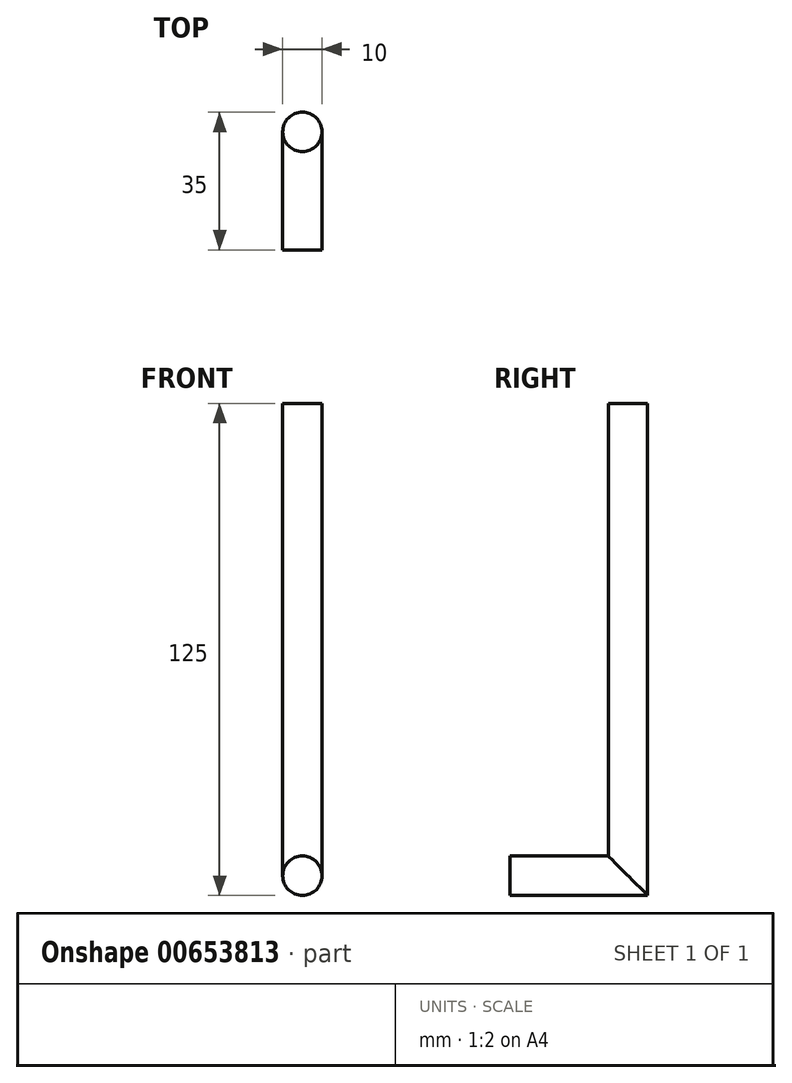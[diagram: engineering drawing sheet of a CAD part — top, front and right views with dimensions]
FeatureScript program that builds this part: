
annotation { "Feature Type Name" : "Feature", "Feature Type Description" : "" }
export const myFeature = defineFeature(function(context is Context, id is Id, definition is map)
    precondition{}
    {
        {
            var Q0;
            Q0=qCreatedBy(makeId("Right.planeOp"),FACE);
            var sketch = newSketch(context, id + "F0", { "sketchPlane" : qUnion([Q0])});
            skLineSegment(sketch, "E0", {"start": v(0, 0) * mm, "end": v(30, 0) * mm});
            skLineSegment(sketch, "E1", {"start": v(30, 0) * mm, "end": v(30, 120) * mm});
            skSolve(sketch);
        }
        {
            var Q0;
            Q0=qCreatedBy(makeId("Front.planeOp"),FACE);
            var sketch = newSketch(context, id + "F1", { "sketchPlane" : qUnion([Q0])});
            skCircle(sketch, "E2", {"center": v(0, 0) * mm, "radius": 5 * mm});
            skSolve(sketch);
        }
        {
            var Q0;
            Q0 = qSketchRegion(id + "F0", true);
            var Q1;
            Q1=makeQuery(id+"F1.imprint","IMPRINT",FACE,{"disambiguationData":[TD([[makeQuery(id+"F1.imprint","IMPRINT",EDGE,{"derivedFrom":sQuery(id+"F1.wireOp",EDGE,"E2")}),1.0]])]});
            var Q2;
            Q2=sQuery(id+"F0.wireOp",EDGE,"E0");
            var Q3;
            Q3=sQuery(id+"F0.wireOp",EDGE,"E1");
            sweep(context, id + "F2", {"profiles" : qUnion([Q0, Q1]), "path" : qUnion([Q2, Q3])});
        }
    });
